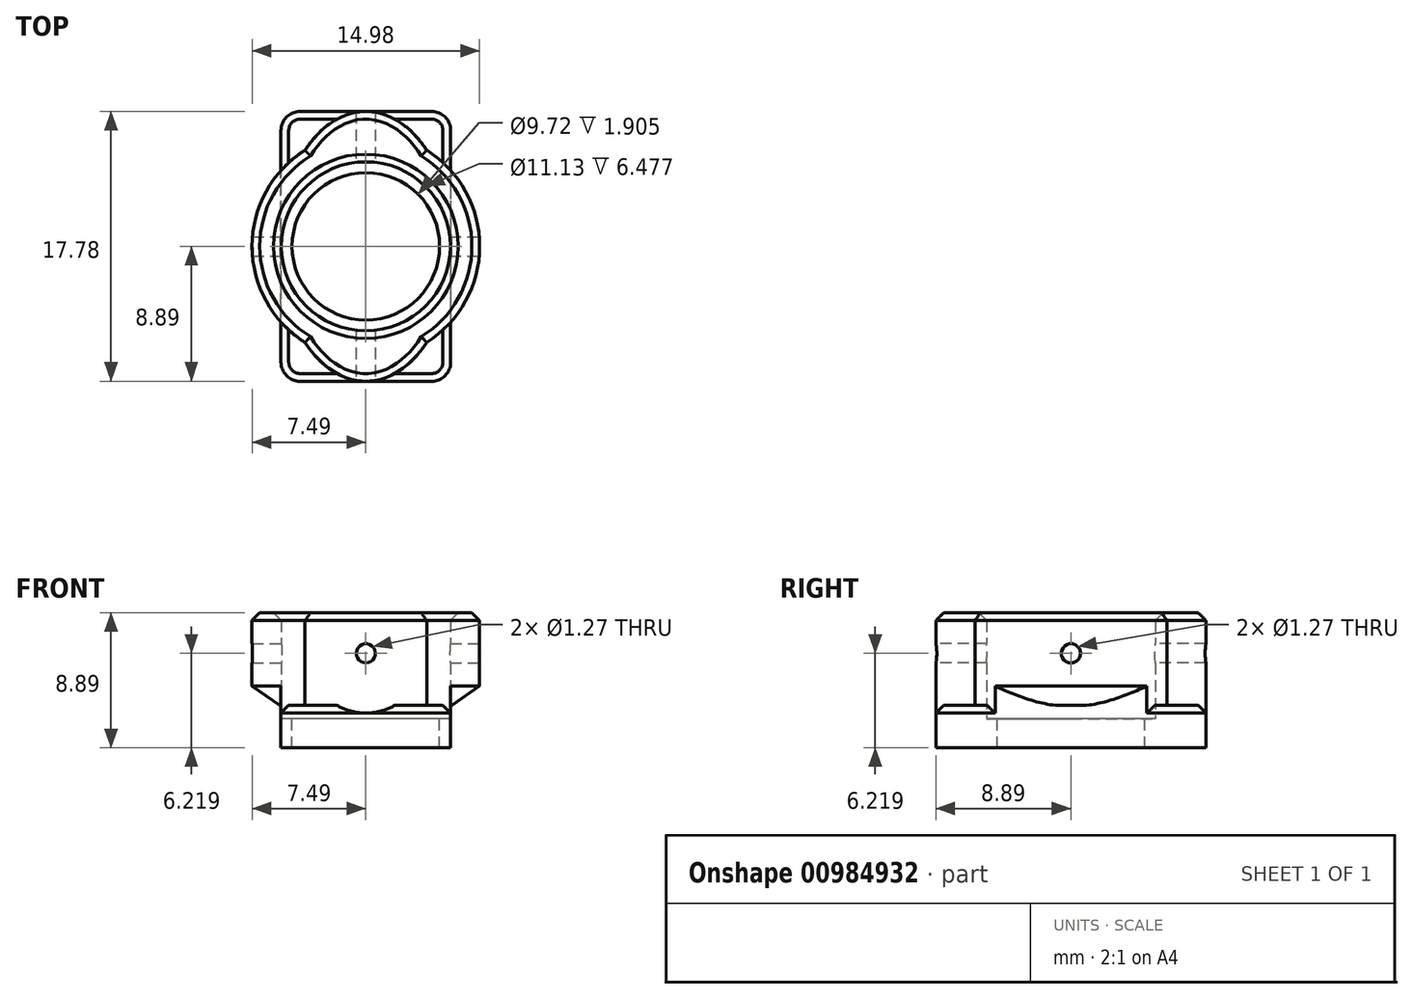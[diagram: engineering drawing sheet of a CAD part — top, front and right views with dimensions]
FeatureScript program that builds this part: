
annotation { "Feature Type Name" : "Feature", "Feature Type Description" : "" }
export const myFeature = defineFeature(function(context is Context, id is Id, definition is map)
    precondition{}
    {
        {
            var Q0;
            Q0=qCreatedBy(makeId("Top.planeOp"),FACE);
            var sketch = newSketch(context, id + "F0", { "sketchPlane" : qUnion([Q0])});
            skPoint(sketch, "E0.middle", {"position": v(0, 0) * mm});
            skCircle(sketch, "E1", {"center": v(0, 0) * mm, "radius": 7.5 * mm});
            skCircle(sketch, "E2", {"center": v(0, 0) * mm, "radius": 5.56 * mm});
            skEllipse(sketch, "E3", {"center": v(0, 0) * mm, "majorRadius": 8.9 * mm, "minorRadius": 5.72 * mm, "majorAxis": v(0, 1)});
            skSolve(sketch);
        }
        {
            var Q0;
            Q0=makeQuery(id+"F0.imprint","IMPRINT",FACE,{"disambiguationData":[TD([[makeQuery(id+"F0.imprint","IMPRINT",EDGE,{"derivedFrom":sQuery(id+"F0.wireOp",EDGE,"E1")}),1.0]])]});
            var Q1;
            {var subQ0=sQuery(id+"F0.wireOp",EDGE,"E3");var subQ1=sQuery(id+"F0.wireOp",EDGE,"E1");var subQ2=makeQuery(id+"F0.imprint","INTERSECT",VERTEX,{"disambiguationData":[OD(0.0)],"derivedFrom":[subQ1,subQ0]});Q1=makeQuery(id+"F0.imprint","IMPRINT",FACE,{"disambiguationData":[TD([[makeQuery(id+"F0.imprint","IMPRINT",EDGE,{"disambiguationData":[TD([[subQ2,1.0]])],"derivedFrom":subQ1}),-1.0]])]});}
            var Q2;
            {var subQ0=sQuery(id+"F0.wireOp",EDGE,"E3");var subQ1=sQuery(id+"F0.wireOp",EDGE,"E1");var subQ2=makeQuery(id+"F0.imprint","INTERSECT",VERTEX,{"disambiguationData":[OD(2.0)],"derivedFrom":[subQ1,subQ0]});Q2=makeQuery(id+"F0.imprint","IMPRINT",FACE,{"disambiguationData":[TD([[makeQuery(id+"F0.imprint","IMPRINT",EDGE,{"disambiguationData":[TD([[subQ2,-1.0]])],"derivedFrom":subQ1}),-1.0]])]});}
            var Q3;
            {var subQ0=sQuery(id+"F0.wireOp",EDGE,"E3");var subQ1=sQuery(id+"F0.wireOp",EDGE,"E1");var subQ2=makeQuery(id+"F0.imprint","INTERSECT",VERTEX,{"disambiguationData":[OD(0.0)],"derivedFrom":[subQ1,subQ0]});Q3=makeQuery(id+"F0.imprint","IMPRINT",FACE,{"disambiguationData":[TD([[makeQuery(id+"F0.imprint","IMPRINT",EDGE,{"disambiguationData":[TD([[subQ2,-1.0]])],"derivedFrom":subQ1}),1.0]])]});}
            var Q4;
            {var subQ0=sQuery(id+"F0.wireOp",EDGE,"E3");var subQ1=sQuery(id+"F0.wireOp",EDGE,"E1");var subQ2=makeQuery(id+"F0.imprint","INTERSECT",VERTEX,{"disambiguationData":[OD(1.0)],"derivedFrom":[subQ1,subQ0]});Q4=makeQuery(id+"F0.imprint","IMPRINT",FACE,{"disambiguationData":[TD([[makeQuery(id+"F0.imprint","IMPRINT",EDGE,{"disambiguationData":[TD([[subQ2,1.0]])],"derivedFrom":subQ1}),1.0]])]});}
            extrude(context, id + "F1", {"entities" : qUnion([Q0, Q1, Q2, Q3, Q4]), "depth" : 6.1 * mm, "offsetDistance" : 25.4 * mm});
        }
        {
            var Q0;
            Q0=qCreatedBy(makeId("Right.planeOp"),FACE);
            var sketch = newSketch(context, id + "F2", { "sketchPlane" : qUnion([Q0])});
            skCircle(sketch, "E4", {"center": v(0, 3.43) * mm, "radius": 0.64 * mm});
            skSolve(sketch);
        }
        {
            var Q0;
            Q0=makeQuery(id+"F2.imprint","IMPRINT",FACE,{"disambiguationData":[TD([[makeQuery(id+"F2.imprint","IMPRINT",EDGE,{"derivedFrom":sQuery(id+"F2.wireOp",EDGE,"E4")}),1.0]])]});
            extrude(context, id + "F3", {"entities" : qUnion([Q0]), "operationType" : NewBodyOperationType.REMOVE, "endBound" : BoundingType.SYMMETRIC, "oppositeDirection" : true, "depth" : 50.8 * mm, "offsetDistance" : 25.4 * mm});
        }
        {
            var Q0;
            Q0=qCreatedBy(makeId("Front.planeOp"),FACE);
            var sketch = newSketch(context, id + "F4", { "sketchPlane" : qUnion([Q0])});
            skCircle(sketch, "E5", {"center": v(0, 3.43) * mm, "radius": 0.64 * mm});
            skSolve(sketch);
        }
        {
            var Q0;
            Q0=qCreatedBy(makeId("Top.planeOp"),FACE);
            var sketch = newSketch(context, id + "F5", { "sketchPlane" : qUnion([Q0])});
            skLineSegment(sketch, "E6.bottom", {"start": v(5.59, 8.9) * mm, "end": v(-5.59, 8.9) * mm});
            skLineSegment(sketch, "E6.top", {"start": v(5.59, -8.9) * mm, "end": v(-5.59, -8.9) * mm});
            skLineSegment(sketch, "E6.left", {"start": v(5.59, 8.9) * mm, "end": v(5.59, -8.9) * mm});
            skLineSegment(sketch, "E6.right", {"start": v(-5.59, 8.9) * mm, "end": v(-5.59, -8.9) * mm});
            skPoint(sketch, "E6.middle", {"position": v(0, 0) * mm});
            skSolve(sketch);
        }
        {
            var Q0;
            Q0=makeQuery(id+"F5.imprint","IMPRINT",FACE,{"disambiguationData":[TD([[makeQuery(id+"F5.imprint","IMPRINT",EDGE,{"derivedFrom":sQuery(id+"F5.wireOp",EDGE,"E6.bottom")}),1.0]])]});
            extrude(context, id + "F6", {"entities" : qUnion([Q0]), "operationType" : NewBodyOperationType.ADD, "oppositeDirection" : true, "depth" : 2.8 * mm, "offsetDistance" : 25.4 * mm});
        }
        {
            var Q0;
            {var subQ0=sQuery(id+"F5.wireOp",EDGE,"E6.left");var subQ1=sQuery(id+"F5.wireOp",EDGE,"E6.bottom");var subQ2=sQuery(id+"F5.wireOp",EDGE,"E6.top");var subQ3=sQuery(id+"F5.wireOp",EDGE,"E6.right");Q0=makeQuery(id+"F6.boolean.opBoolean","SPLIT",FACE,{"disambiguationData":[TD([makeQuery(id+"F1.opExtrude","SWEPT_FACE",FACE,{"disambiguationData":[OSD([sQuery(id+"F0.wireOp",EDGE,"E1")])]})])],"derivedFrom":makeQuery(id+"F6.opExtrude","CAP_FACE",FACE,{"disambiguationData":[OSD([subQ1,subQ2,subQ0,subQ3])],"isStart":true})});}
            var sketch = newSketch(context, id + "F7", { "sketchPlane" : qUnion([Q0])});
            skCircle(sketch, "E7", {"center": v(0, 0) * mm, "radius": 4.86 * mm});
            skCircle(sketch, "E8", {"center": v(0, 0) * mm, "radius": 5.56 * mm});
            skSolve(sketch);
        }
        {
            var Q0;
            Q0=makeQuery(id+"F7.imprint","IMPRINT",FACE,{"disambiguationData":[TD([[makeQuery(id+"F7.imprint","IMPRINT",EDGE,{"derivedFrom":sQuery(id+"F7.wireOp",EDGE,"E7")}),1.0]])]});
            extrude(context, id + "F8", {"entities" : qUnion([Q0]), "operationType" : NewBodyOperationType.REMOVE, "oppositeDirection" : true, "depth" : 2.8 * mm, "offsetDistance" : 25.4 * mm});
        }
        {
            var Q0;
            Q0=makeQuery(id+"F7.imprint","IMPRINT",FACE,{"disambiguationData":[TD([[makeQuery(id+"F7.imprint","IMPRINT",EDGE,{"derivedFrom":sQuery(id+"F7.wireOp",EDGE,"E7")}),-1.0]])]});
            extrude(context, id + "F9", {"entities" : qUnion([Q0]), "operationType" : NewBodyOperationType.REMOVE, "oppositeDirection" : true, "depth" : 0.89 * mm, "offsetDistance" : 25.4 * mm});
        }
        {
            var Q0;
            Q0=makeQuery(id+"F6.opExtrude","SWEPT_EDGE",EDGE,{"disambiguationData":[OSD([sQuery(id+"F5.wireOp",EDGE,"E6.bottom"),sQuery(id+"F5.wireOp",EDGE,"E6.left")])]});
            var Q1;
            Q1=makeQuery(id+"F6.opExtrude","SWEPT_EDGE",EDGE,{"disambiguationData":[OSD([sQuery(id+"F5.wireOp",EDGE,"E6.bottom"),sQuery(id+"F5.wireOp",EDGE,"E6.right")])]});
            var Q2;
            Q2=makeQuery(id+"F6.opExtrude","SWEPT_EDGE",EDGE,{"disambiguationData":[OSD([sQuery(id+"F5.wireOp",EDGE,"E6.top"),sQuery(id+"F5.wireOp",EDGE,"E6.right")])]});
            var Q3;
            Q3=makeQuery(id+"F6.opExtrude","SWEPT_EDGE",EDGE,{"disambiguationData":[OSD([sQuery(id+"F5.wireOp",EDGE,"E6.top"),sQuery(id+"F5.wireOp",EDGE,"E6.left")])]});
            fillet(context, id + "F10", {"entities" : qUnion([Q0, Q1, Q2, Q3]), "radius" : 1.27 * mm, "tangentPropagation" : true, "allowEdgeOverflow" : false});
        }
        {
            var Q0;
            {var subQ0=sQuery(id+"F0.wireOp",EDGE,"E3");var subQ1=sQuery(id+"F0.wireOp",EDGE,"E1");Q0=makeQuery(id+"F1.opExtrude","CAP_EDGE",EDGE,{"disambiguationData":[OSD([subQ0]),TDD([makeQuery(id+"F0.imprint","IMPRINT",EDGE,{"disambiguationData":[TD([[makeQuery(id+"F0.imprint","INTERSECT",VERTEX,{"disambiguationData":[OD(2.0)],"derivedFrom":[subQ1,subQ0]}),-1.0]])],"derivedFrom":subQ0})])],"isStart":false});}
            var Q1;
            {var subQ0=sQuery(id+"F0.wireOp",EDGE,"E3");var subQ1=sQuery(id+"F0.wireOp",EDGE,"E1");Q1=makeQuery(id+"F1.opExtrude","CAP_EDGE",EDGE,{"disambiguationData":[OSD([subQ0]),TDD([makeQuery(id+"F0.imprint","IMPRINT",EDGE,{"disambiguationData":[TD([[makeQuery(id+"F0.imprint","INTERSECT",VERTEX,{"disambiguationData":[OD(0.0)],"derivedFrom":[subQ1,subQ0]}),1.0]])],"derivedFrom":subQ0})])],"isStart":false});}
            var Q2;
            {var subQ0=sQuery(id+"F0.wireOp",EDGE,"E3");var subQ1=sQuery(id+"F0.wireOp",EDGE,"E1");Q2=makeQuery(id+"F1.opExtrude","CAP_EDGE",EDGE,{"disambiguationData":[OSD([subQ1]),TDD([makeQuery(id+"F0.imprint","IMPRINT",EDGE,{"disambiguationData":[TD([[makeQuery(id+"F0.imprint","INTERSECT",VERTEX,{"disambiguationData":[OD(1.0)],"derivedFrom":[subQ1,subQ0]}),1.0]])],"derivedFrom":subQ1})])],"isStart":false});}
            var Q3;
            {var subQ0=sQuery(id+"F0.wireOp",EDGE,"E3");var subQ1=sQuery(id+"F0.wireOp",EDGE,"E1");Q3=makeQuery(id+"F1.opExtrude","CAP_EDGE",EDGE,{"disambiguationData":[OSD([subQ1]),TDD([makeQuery(id+"F0.imprint","IMPRINT",EDGE,{"disambiguationData":[TD([[makeQuery(id+"F0.imprint","INTERSECT",VERTEX,{"disambiguationData":[OD(0.0)],"derivedFrom":[subQ1,subQ0]}),-1.0]])],"derivedFrom":subQ1})])],"isStart":false});}
            var Q4;
            Q4=makeQuery(id+"F1.opExtrude","CAP_EDGE",EDGE,{"disambiguationData":[OSD([sQuery(id+"F0.wireOp",EDGE,"E2")])],"isStart":false});
            var Q5;
            {var subQ0=sQuery(id+"F5.wireOp",EDGE,"E6.top");var subQ1=sQuery(id+"F5.wireOp",EDGE,"E6.right");var subQ2=makeQuery(id+"F6.opExtrude","CAP_FACE",FACE,{"disambiguationData":[OSD([sQuery(id+"F5.wireOp",EDGE,"E6.bottom"),subQ0,sQuery(id+"F5.wireOp",EDGE,"E6.left"),subQ1])],"isStart":true});var subQ5=makeQuery(id+"F6.opExtrude","SWEPT_FACE",FACE,{"disambiguationData":[OSD([subQ1])]});Q5=makeQuery(id+"F6.boolean.opBoolean","SPLIT",EDGE,{"disambiguationData":[topologyDisambiguationEdgeConnected([subQ2,subQ5]),TD([makeQuery(id+"F6.opExtrude","SWEPT_FACE",FACE,{"disambiguationData":[OSD([subQ0])]})])],"derivedFrom":makeQuery(id+"F6.opExtrude","CAP_EDGE",EDGE,{"disambiguationData":[OSD([subQ1])],"isStart":true})});}
            var Q6;
            {var subQ0=sQuery(id+"F5.wireOp",EDGE,"E6.bottom");var subQ3=sQuery(id+"F5.wireOp",EDGE,"E6.left");var subQ4=makeQuery(id+"F6.opExtrude","CAP_FACE",FACE,{"disambiguationData":[OSD([subQ0,sQuery(id+"F5.wireOp",EDGE,"E6.top"),subQ3,sQuery(id+"F5.wireOp",EDGE,"E6.right")])],"isStart":true});var subQ5=makeQuery(id+"F6.opExtrude","SWEPT_FACE",FACE,{"disambiguationData":[OSD([subQ3])]});Q6=makeQuery(id+"F6.boolean.opBoolean","SPLIT",EDGE,{"disambiguationData":[topologyDisambiguationEdgeConnected([subQ4,subQ5]),TD([makeQuery(id+"F6.opExtrude","SWEPT_FACE",FACE,{"disambiguationData":[OSD([subQ0])]})])],"derivedFrom":makeQuery(id+"F6.opExtrude","CAP_EDGE",EDGE,{"disambiguationData":[OSD([subQ3])],"isStart":true})});}
            chamfer(context, id + "F11", {"entities" : qUnion([Q0, Q1, Q2, Q3, Q4, Q5, Q6]), "width" : 0.5 * mm, "tangentPropagation" : true});
        }
        {
            var Q0;
            Q0=makeQuery(id+"F4.imprint","IMPRINT",FACE,{"disambiguationData":[TD([[makeQuery(id+"F4.imprint","IMPRINT",EDGE,{"derivedFrom":sQuery(id+"F4.wireOp",EDGE,"E5")}),1.0]])]});
            extrude(context, id + "F12", {"entities" : qUnion([Q0]), "operationType" : NewBodyOperationType.REMOVE, "endBound" : BoundingType.SYMMETRIC, "oppositeDirection" : true, "depth" : 25.4 * mm, "offsetDistance" : 25.4 * mm});
        }
        {
            var Q0;
            {var subQ0=sQuery(id+"F0.wireOp",EDGE,"E3");var subQ1=sQuery(id+"F0.wireOp",EDGE,"E1");var subQ2=makeQuery(id+"F0.imprint","IMPRINT",EDGE,{"disambiguationData":[TD([[makeQuery(id+"F0.imprint","INTERSECT",VERTEX,{"disambiguationData":[OD(1.0)],"derivedFrom":[subQ1,subQ0]}),1.0]])],"derivedFrom":subQ1});Q0=makeQuery(id+"F6.boolean.opBoolean","SPLIT",EDGE,{"disambiguationData":[topologyDisambiguationEdgeConnected([makeQuery(id+"F1.opExtrude","CAP_FACE",FACE,{"disambiguationData":[OSD([subQ1,sQuery(id+"F0.wireOp",EDGE,"E2"),subQ0])],"isStart":true}),makeQuery(id+"F1.opExtrude","SWEPT_FACE",FACE,{"disambiguationData":[OSD([subQ1]),TDD([subQ2])]})])],"derivedFrom":makeQuery(id+"F1.opExtrude","CAP_EDGE",EDGE,{"disambiguationData":[OSD([subQ1]),TDD([subQ2])],"isStart":true})});}
            var Q1;
            {var subQ0=sQuery(id+"F0.wireOp",EDGE,"E3");var subQ1=sQuery(id+"F0.wireOp",EDGE,"E1");var subQ2=makeQuery(id+"F0.imprint","IMPRINT",EDGE,{"disambiguationData":[TD([[makeQuery(id+"F0.imprint","INTERSECT",VERTEX,{"disambiguationData":[OD(0.0)],"derivedFrom":[subQ1,subQ0]}),-1.0]])],"derivedFrom":subQ1});Q1=makeQuery(id+"F6.boolean.opBoolean","SPLIT",EDGE,{"disambiguationData":[topologyDisambiguationEdgeConnected([makeQuery(id+"F1.opExtrude","SWEPT_FACE",FACE,{"disambiguationData":[OSD([subQ1]),TDD([subQ2])]}),makeQuery(id+"F1.opExtrude","CAP_FACE",FACE,{"disambiguationData":[OSD([subQ1,sQuery(id+"F0.wireOp",EDGE,"E2"),subQ0])],"isStart":true})])],"derivedFrom":makeQuery(id+"F1.opExtrude","CAP_EDGE",EDGE,{"disambiguationData":[OSD([subQ1]),TDD([subQ2])],"isStart":true})});}
            chamfer(context, id + "F13", {"entities" : qUnion([Q0, Q1]), "chamferType" : ChamferType.OFFSET_ANGLE, "width" : 1.27 * mm, "oppositeDirection" : false, "angle" : 55 * degree, "tangentPropagation" : true});
        }
    });
